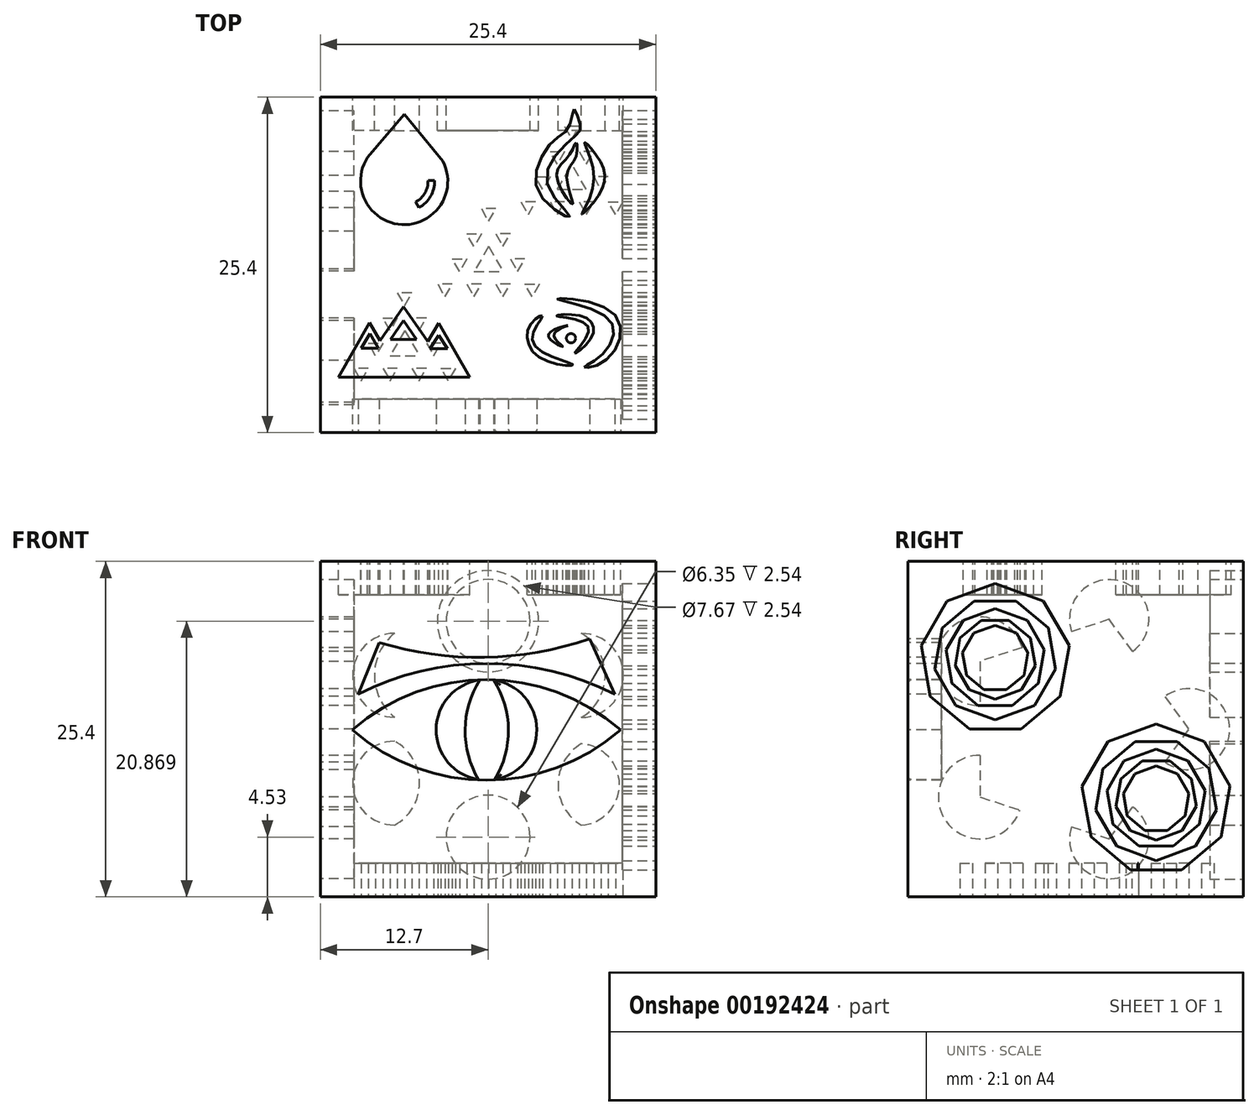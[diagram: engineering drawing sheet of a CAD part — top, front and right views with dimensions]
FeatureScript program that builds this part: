
annotation { "Feature Type Name" : "Feature", "Feature Type Description" : "" }
export const myFeature = defineFeature(function(context is Context, id is Id, definition is map)
    precondition{}
    {
        {
            var Q0;
            Q0=qCreatedBy(makeId("Front.planeOp"),FACE);
            var sketch = newSketch(context, id + "F0", { "sketchPlane" : qUnion([Q0])});
            skLineSegment(sketch, "E0.bottom", {"start": v(12.7, -12.7) * mm, "end": v(-12.7, -12.7) * mm});
            skLineSegment(sketch, "E0.top", {"start": v(12.7, 12.7) * mm, "end": v(-12.7, 12.7) * mm});
            skLineSegment(sketch, "E0.left", {"start": v(12.7, -12.7) * mm, "end": v(12.7, 12.7) * mm});
            skLineSegment(sketch, "E0.right", {"start": v(-12.7, -12.7) * mm, "end": v(-12.7, 12.7) * mm});
            skSolve(sketch);
        }
        {
            var Q0;
            Q0=makeQuery(id+"F0.imprint","IMPRINT",FACE,{"disambiguationData":[TD([[makeQuery(id+"F0.imprint","IMPRINT",EDGE,{"derivedFrom":sQuery(id+"F0.wireOp",EDGE,"E0.bottom")}),-1.0]])]});
            extrude(context, id + "F1", {"entities" : qUnion([Q0]), "depth" : 25.4 * mm});
        }
        {
            var Q0;
            Q0=makeQuery(id+"F1.opExtrude","SWEPT_FACE",FACE,{"disambiguationData":[OSD([sQuery(id+"F0.wireOp",EDGE,"E0.left")])]});
            var sketch = newSketch(context, id + "F2", { "sketchPlane" : qUnion([Q0])});
            skPoint(sketch, "E1.0.midPoint", {"position": v(-14.15, 6.32) * mm});
            skLineSegment(sketch, "E2.0", {"start": v(-2.95, -0.95) * mm, "end": v(-1, -4.32) * mm});
            skLineSegment(sketch, "E2.1", {"start": v(-1, -4.32) * mm, "end": v(-1.67, -8.15) * mm});
            skLineSegment(sketch, "E2.2", {"start": v(-1.67, -8.15) * mm, "end": v(-4.65, -10.65) * mm});
            skLineSegment(sketch, "E2.3", {"start": v(-4.65, -10.65) * mm, "end": v(-8.55, -10.65) * mm});
            skLineSegment(sketch, "E2.4", {"start": v(-8.55, -10.65) * mm, "end": v(-11.53, -8.15) * mm});
            skLineSegment(sketch, "E2.5", {"start": v(-11.53, -8.15) * mm, "end": v(-12.2, -4.32) * mm});
            skLineSegment(sketch, "E2.6", {"start": v(-12.2, -4.32) * mm, "end": v(-10.26, -0.95) * mm});
            skLineSegment(sketch, "E2.7", {"start": v(-10.26, -0.95) * mm, "end": v(-6.6, 0.38) * mm});
            skLineSegment(sketch, "E2.8", {"start": v(-6.6, 0.38) * mm, "end": v(-2.95, -0.95) * mm});
            skPoint(sketch, "E2.0.midPoint", {"position": v(-1.97, -2.63) * mm});
            skLineSegment(sketch, "E3", {"start": v(-5.02, -0.95) * mm, "end": v(-2.59, -2.99) * mm});
            skLineSegment(sketch, "E4", {"start": v(-2.03, -6.11) * mm, "end": v(-2.59, -2.99) * mm});
            skLineSegment(sketch, "E5", {"start": v(-3.62, -8.86) * mm, "end": v(-6.6, -9.95) * mm});
            skLineSegment(sketch, "E6", {"start": v(-2.03, -6.11) * mm, "end": v(-3.62, -8.86) * mm});
            skLineSegment(sketch, "E7", {"start": v(-6.6, -9.95) * mm, "end": v(-9.58, -8.86) * mm});
            skLineSegment(sketch, "E8", {"start": v(-11.17, -6.11) * mm, "end": v(-9.58, -8.86) * mm});
            skLineSegment(sketch, "E9", {"start": v(-11.17, -6.11) * mm, "end": v(-10.62, -3) * mm});
            skLineSegment(sketch, "E10", {"start": v(-8.19, -0.95) * mm, "end": v(-10.62, -3) * mm});
            skLineSegment(sketch, "E11", {"start": v(-8.19, -0.95) * mm, "end": v(-5.02, -0.95) * mm});
            skLineSegment(sketch, "E12", {"start": v(-6.6, -1.53) * mm, "end": v(-4.17, -2.4) * mm});
            skLineSegment(sketch, "E13", {"start": v(-4.17, -2.4) * mm, "end": v(-2.88, -4.65) * mm});
            skLineSegment(sketch, "E14", {"start": v(-3.33, -7.2) * mm, "end": v(-5.3, -8.86) * mm});
            skLineSegment(sketch, "E15", {"start": v(-7.9, -8.86) * mm, "end": v(-9.88, -7.2) * mm});
            skLineSegment(sketch, "E16", {"start": v(-10.33, -4.65) * mm, "end": v(-9.03, -2.41) * mm});
            skLineSegment(sketch, "E17", {"start": v(-9.03, -2.41) * mm, "end": v(-6.6, -1.53) * mm});
            skLineSegment(sketch, "E18", {"start": v(-5.3, -8.86) * mm, "end": v(-7.9, -8.86) * mm});
            skLineSegment(sketch, "E19", {"start": v(-9.88, -7.2) * mm, "end": v(-10.33, -4.65) * mm});
            skLineSegment(sketch, "E20", {"start": v(-2.88, -4.65) * mm, "end": v(-3.33, -7.2) * mm});
            skLineSegment(sketch, "E21", {"start": v(-7.66, -2.41) * mm, "end": v(-5.55, -2.41) * mm});
            skLineSegment(sketch, "E22", {"start": v(-3.93, -3.77) * mm, "end": v(-3.57, -5.84) * mm});
            skLineSegment(sketch, "E23", {"start": v(-4.62, -7.67) * mm, "end": v(-6.6, -8.39) * mm});
            skLineSegment(sketch, "E24", {"start": v(-7.9, -8.86) * mm, "end": v(-7.9, -8.86) * mm});
            skLineSegment(sketch, "E25", {"start": v(-9.27, -3.76) * mm, "end": v(-7.66, -2.41) * mm});
            skLineSegment(sketch, "E26", {"start": v(-6.6, -1.53) * mm, "end": v(-6.6, -1.53) * mm});
            skLineSegment(sketch, "E27", {"start": v(-3.57, -5.84) * mm, "end": v(-4.62, -7.67) * mm});
            skLineSegment(sketch, "E28", {"start": v(-6.6, -8.39) * mm, "end": v(-8.58, -7.67) * mm});
            skLineSegment(sketch, "E29", {"start": v(-9.63, -5.85) * mm, "end": v(-9.27, -3.76) * mm});
            skLineSegment(sketch, "E30", {"start": v(-6.6, -2.8) * mm, "end": v(-4.99, -3.38) * mm});
            skLineSegment(sketch, "E31", {"start": v(-4.13, -4.87) * mm, "end": v(-4.42, -6.56) * mm});
            skLineSegment(sketch, "E32", {"start": v(-5.74, -7.67) * mm, "end": v(-7.46, -7.67) * mm});
            skLineSegment(sketch, "E33", {"start": v(-8.78, -6.57) * mm, "end": v(-9.07, -4.87) * mm});
            skLineSegment(sketch, "E34", {"start": v(-8.22, -3.38) * mm, "end": v(-6.6, -2.8) * mm});
            skLineSegment(sketch, "E35", {"start": v(-4.99, -3.38) * mm, "end": v(-4.13, -4.87) * mm});
            skLineSegment(sketch, "E36", {"start": v(-4.42, -6.56) * mm, "end": v(-5.74, -7.67) * mm});
            skLineSegment(sketch, "E37", {"start": v(-7.46, -7.67) * mm, "end": v(-8.78, -6.57) * mm});
            skLineSegment(sketch, "E38", {"start": v(-9.07, -4.87) * mm, "end": v(-8.22, -3.38) * mm});
            skLineSegment(sketch, "E39.0", {"start": v(-15.13, 9.7) * mm, "end": v(-13.18, 6.34) * mm});
            skLineSegment(sketch, "E39.1", {"start": v(-13.18, 6.34) * mm, "end": v(-13.86, 2.5) * mm});
            skLineSegment(sketch, "E39.2", {"start": v(-13.86, 2.5) * mm, "end": v(-16.84, 0) * mm});
            skLineSegment(sketch, "E39.3", {"start": v(-16.84, 0) * mm, "end": v(-20.73, 0) * mm});
            skLineSegment(sketch, "E39.4", {"start": v(-20.73, 0) * mm, "end": v(-23.71, 2.5) * mm});
            skLineSegment(sketch, "E39.5", {"start": v(-23.71, 2.5) * mm, "end": v(-24.4, 6.33) * mm});
            skLineSegment(sketch, "E39.6", {"start": v(-24.4, 6.33) * mm, "end": v(-22.45, 9.7) * mm});
            skLineSegment(sketch, "E39.7", {"start": v(-22.45, 9.7) * mm, "end": v(-18.79, 11.04) * mm});
            skLineSegment(sketch, "E39.8", {"start": v(-18.79, 11.04) * mm, "end": v(-15.13, 9.7) * mm});
            skPoint(sketch, "E39.0.midPoint", {"position": v(-14.16, 8.02) * mm});
            skLineSegment(sketch, "E40", {"start": v(-17.2, 9.7) * mm, "end": v(-14.77, 7.67) * mm});
            skLineSegment(sketch, "E41", {"start": v(-14.22, 4.54) * mm, "end": v(-14.77, 7.67) * mm});
            skLineSegment(sketch, "E42", {"start": v(-15.8, 1.8) * mm, "end": v(-18.78, 0.7) * mm});
            skLineSegment(sketch, "E43", {"start": v(-14.22, 4.54) * mm, "end": v(-15.8, 1.8) * mm});
            skLineSegment(sketch, "E44", {"start": v(-18.78, 0.7) * mm, "end": v(-21.77, 1.8) * mm});
            skLineSegment(sketch, "E45", {"start": v(-23.35, 4.54) * mm, "end": v(-21.77, 1.8) * mm});
            skLineSegment(sketch, "E46", {"start": v(-23.35, 4.54) * mm, "end": v(-23.35, 4.54) * mm});
            skLineSegment(sketch, "E47", {"start": v(-20.37, 9.7) * mm, "end": v(-17.2, 9.7) * mm});
            skLineSegment(sketch, "E48", {"start": v(-18.79, 9.13) * mm, "end": v(-16.36, 8.24) * mm});
            skLineSegment(sketch, "E49", {"start": v(-16.36, 8.24) * mm, "end": v(-15.06, 6) * mm});
            skLineSegment(sketch, "E50", {"start": v(-22.51, 6) * mm, "end": v(-21.22, 8.24) * mm});
            skLineSegment(sketch, "E51", {"start": v(-21.22, 8.24) * mm, "end": v(-18.79, 9.13) * mm});
            skLineSegment(sketch, "E52", {"start": v(-22.06, 3.46) * mm, "end": v(-22.51, 6) * mm});
            skLineSegment(sketch, "E53", {"start": v(-15.06, 6) * mm, "end": v(-15.51, 3.46) * mm});
            skLineSegment(sketch, "E54", {"start": v(-19.85, 8.24) * mm, "end": v(-17.73, 8.24) * mm});
            skLineSegment(sketch, "E55", {"start": v(-16.12, 6.89) * mm, "end": v(-15.75, 4.81) * mm});
            skLineSegment(sketch, "E56", {"start": v(-16.8, 2.99) * mm, "end": v(-18.78, 2.26) * mm});
            skLineSegment(sketch, "E57", {"start": v(-21.46, 6.89) * mm, "end": v(-19.85, 8.24) * mm});
            skLineSegment(sketch, "E58", {"start": v(-15.75, 4.81) * mm, "end": v(-16.8, 2.99) * mm});
            skLineSegment(sketch, "E59", {"start": v(-18.78, 2.26) * mm, "end": v(-20.77, 2.99) * mm});
            skLineSegment(sketch, "E60", {"start": v(-21.82, 4.8) * mm, "end": v(-21.46, 6.89) * mm});
            skLineSegment(sketch, "E61", {"start": v(-18.79, 7.86) * mm, "end": v(-17.17, 7.27) * mm});
            skLineSegment(sketch, "E62", {"start": v(-16.31, 5.78) * mm, "end": v(-16.6, 4.1) * mm});
            skLineSegment(sketch, "E63", {"start": v(-17.93, 2.99) * mm, "end": v(-19.64, 2.99) * mm});
            skLineSegment(sketch, "E64", {"start": v(-20.96, 4.09) * mm, "end": v(-21.26, 5.78) * mm});
            skLineSegment(sketch, "E65", {"start": v(-17.17, 7.27) * mm, "end": v(-16.31, 5.78) * mm});
            skLineSegment(sketch, "E66", {"start": v(-16.6, 4.1) * mm, "end": v(-17.93, 2.99) * mm});
            skLineSegment(sketch, "E67", {"start": v(-19.64, 2.99) * mm, "end": v(-20.96, 4.09) * mm});
            skLineSegment(sketch, "E68", {"start": v(-21.26, 5.78) * mm, "end": v(-20.4, 7.27) * mm});
            skPoint(sketch, "E69.endSnap0", {"position": v(-6.6, -8.86) * mm});
            skPoint(sketch, "E70.orphan", {"position": v(-11.17, -6.11) * mm});
            skPoint(sketch, "E71.orphan", {"position": v(-9.58, -8.86) * mm});
            skLineSegment(sketch, "E72.trimOffspring", {"start": v(-7.89, -8.86) * mm, "end": v(-7.9, -8.86) * mm});
            skLineSegment(sketch, "E73.trimOffspring", {"start": v(-8.58, -7.67) * mm, "end": v(-9.63, -5.85) * mm});
            skLineSegment(sketch, "E74.trimOffspring", {"start": v(-5.55, -2.41) * mm, "end": v(-3.93, -3.77) * mm});
            skLineSegment(sketch, "E75", {"start": v(-20.37, 9.7) * mm, "end": v(-22.8, 7.66) * mm});
            skLineSegment(sketch, "E76", {"start": v(-23.35, 4.54) * mm, "end": v(-22.8, 7.66) * mm});
            skLineSegment(sketch, "E77.trimOffspring", {"start": v(-20.77, 2.99) * mm, "end": v(-21.82, 4.8) * mm});
            skLineSegment(sketch, "E78.trimOffspring", {"start": v(-17.73, 8.24) * mm, "end": v(-16.12, 6.89) * mm});
            skLineSegment(sketch, "E79", {"start": v(-20.4, 7.27) * mm, "end": v(-18.79, 7.86) * mm});
            skLineSegment(sketch, "E80", {"start": v(-22.06, 3.46) * mm, "end": v(-20.08, 1.8) * mm});
            skLineSegment(sketch, "E81", {"start": v(-20.08, 1.8) * mm, "end": v(-17.5, 1.8) * mm});
            skLineSegment(sketch, "E82", {"start": v(-15.51, 3.46) * mm, "end": v(-17.5, 1.8) * mm});
            skSolve(sketch);
        }
        {
            var Q0;
            Q0=makeQuery(id+"F2.imprint","IMPRINT",FACE,{"disambiguationData":[TD([[makeQuery(id+"F2.imprint","IMPRINT",EDGE,{"derivedFrom":sQuery(id+"F2.wireOp",EDGE,"E2.0")}),-1.0]])]});
            var Q1;
            {var subQ10=sQuery(id+"F2.wireOp",EDGE,"E13");Q1=makeQuery(id+"F2.imprint","IMPRINT",FACE,{"disambiguationData":[TD([[makeQuery(id+"F2.imprint","IMPRINT",EDGE,{"derivedFrom":subQ10}),-1.0]])]});}
            var Q2;
            Q2=makeQuery(id+"F2.imprint","IMPRINT",FACE,{"disambiguationData":[TD([[makeQuery(id+"F2.imprint","IMPRINT",EDGE,{"derivedFrom":sQuery(id+"F2.wireOp",EDGE,"E30")}),-1.0]])]});
            extrude(context, id + "F3", {"entities" : qUnion([Q0, Q1, Q2]), "operationType" : NewBodyOperationType.REMOVE, "oppositeDirection" : true, "depth" : 2.54 * mm});
        }
        {
            var Q0;
            Q0=makeQuery(id+"F2.imprint","IMPRINT",FACE,{"disambiguationData":[TD([[makeQuery(id+"F2.imprint","IMPRINT",EDGE,{"derivedFrom":sQuery(id+"F2.wireOp",EDGE,"E39.0")}),-1.0]])]});
            var Q1;
            Q1=makeQuery(id+"F2.imprint","IMPRINT",FACE,{"disambiguationData":[TD([[makeQuery(id+"F2.imprint","IMPRINT",EDGE,{"derivedFrom":sQuery(id+"F2.wireOp",EDGE,"E48")}),-1.0]])]});
            var Q2;
            Q2=makeQuery(id+"F2.imprint","IMPRINT",FACE,{"disambiguationData":[TD([[makeQuery(id+"F2.imprint","IMPRINT",EDGE,{"derivedFrom":sQuery(id+"F2.wireOp",EDGE,"E61")}),-1.0]])]});
            extrude(context, id + "F4", {"entities" : qUnion([Q0, Q1, Q2]), "operationType" : NewBodyOperationType.REMOVE, "oppositeDirection" : true, "depth" : 2.54 * mm});
        }
        {
            var Q0;
            {var subQ0=sQuery(id+"F0.wireOp",EDGE,"Xz3h7y4A-9vBR-dhRj-rXEC-ED03mauQ3q4K");var subQ1=sQuery(id+"F0.wireOp",EDGE,"V4NEk3Ng-o78i-laLm-4UWv-CYlOKSxuC9OK");var subQ2=sQuery(id+"F0.wireOp",EDGE,"mu0T6BV1-LyfI-ftHM-lo53-aBSG0DslEf0h");var subQ3=sQuery(id+"F0.wireOp",EDGE,"n15qH9Pv-QceR-e55J-xRJA-4Z23myPxkwqh");var subQ4=makeQuery(id+"F0.imprint","INTERSECT",VERTEX,{"derivedFrom":[subQ3,subQ2,subQ1,subQ0]});var subQ5=sQuery(id+"F0.wireOp",EDGE,"ffxhiTFt-cJhM-8va8-o5as-TkoKFeYBlZlv");var subQ7=makeQuery(id+"F0.imprint","INTERSECT",VERTEX,{"disambiguationData":[OD(1.0)],"derivedFrom":[subQ5,subQ3]});var subQ8=makeQuery(id+"F0.imprint","INTERSECT",VERTEX,{"disambiguationData":[OD(0.0)],"derivedFrom":[subQ5,subQ3]});var subQ9=sQuery(id+"F0.wireOp",EDGE,"c9E78YFX-uoQ2-b4qo-jO5v-nr7yERCXFzAn");var subQ10=sQuery(id+"F0.wireOp",EDGE,"twlR4qeh-pLNo-oQQC-zrHb-Cr716ABeDlEO");var subQ11=sQuery(id+"F0.wireOp",EDGE,"i75eDPNT-zkQp-M9GV-G1os-5atVE6ZioN9H");var subQ12=sQuery(id+"F0.wireOp",EDGE,"Tw14qS9G-7LKB-szX9-mnEh-GGdI6fmKwQ57");Q0=makeQuery(id+"FcBMYDftipxSYez_0.boolean.opBoolean","MERGE",FACE,{"derivedFrom":[makeQuery(id+"FdykabLyeeUPw6N_0.boolean.opBoolean","MERGE",FACE,{"derivedFrom":[makeQuery(id+"F1.opExtrude","CAP_FACE",FACE,{"disambiguationData":[OSD([sQuery(id+"F0.wireOp",EDGE,"E0.bottom"),sQuery(id+"F0.wireOp",EDGE,"E0.top"),sQuery(id+"F0.wireOp",EDGE,"E0.left"),sQuery(id+"F0.wireOp",EDGE,"E0.right"),subQ5,subQ3,subQ12,subQ11,subQ10,subQ9])],"isStart":true}),makeQuery(id+"FdykabLyeeUPw6N_0.opExtrude","CAP_FACE",FACE,{"disambiguationData":[OSD([subQ12,subQ11,subQ10,subQ9])],"isStart":true})]}),makeQuery(id+"FcBMYDftipxSYez_0.opExtrude","CAP_FACE",FACE,{"disambiguationData":[OSD([subQ5,subQ3,subQ2]),TDD([makeQuery(id+"F0.imprint","IMPRINT",EDGE,{"disambiguationData":[TD([[subQ8,-1.0]])],"derivedFrom":subQ5}),makeQuery(id+"F0.imprint","IMPRINT",EDGE,{"disambiguationData":[TD([[subQ8,1.0]])],"derivedFrom":subQ3}),makeQuery(id+"F0.imprint","IMPRINT",EDGE,{"disambiguationData":[TD([[subQ4,-1.0]])],"derivedFrom":subQ2})])],"isStart":true}),makeQuery(id+"FcBMYDftipxSYez_0.opExtrude","CAP_FACE",FACE,{"disambiguationData":[OSD([subQ5,subQ3,subQ2]),TDD([makeQuery(id+"F0.imprint","IMPRINT",EDGE,{"disambiguationData":[TD([[subQ7,1.0]])],"derivedFrom":subQ5}),makeQuery(id+"F0.imprint","IMPRINT",EDGE,{"disambiguationData":[TD([[subQ7,-1.0]])],"derivedFrom":subQ3}),makeQuery(id+"F0.imprint","IMPRINT",EDGE,{"disambiguationData":[TD([[subQ4,1.0]])],"derivedFrom":subQ2})])],"isStart":true})]});}
            var sketch = newSketch(context, id + "F5", { "sketchPlane" : qUnion([Q0])});
            skPoint(sketch, "E83.cCircle.perimeterSnap0", {"position": v(12.7, 0) * mm});
            skPoint(sketch, "E83.0.midPoint", {"position": v(7.08, 0) * mm});
            skPoint(sketch, "E83.0.midPoint.positionSnap0", {"position": v(12.7, 0) * mm});
            skCircle(sketch, "E84", {"center": v(0, 8.17) * mm, "radius": 3.17 * mm});
            skCircle(sketch, "E85", {"center": v(7.08, 4.08) * mm, "radius": 3.18 * mm});
            skCircle(sketch, "E86", {"center": v(7.08, -4.08) * mm, "radius": 3.18 * mm});
            skCircle(sketch, "E87", {"center": v(0, -8.17) * mm, "radius": 3.18 * mm});
            skCircle(sketch, "E88", {"center": v(-6.87, -4.19) * mm, "radius": 3.08 * mm});
            skCircle(sketch, "E89", {"center": v(-7.08, 4.07) * mm, "radius": 3.18 * mm});
            skArc(sketch, "E90", {"start": v(7.08, 0.9) * mm, "mid": v(8.6, 4.08) * mm, "end": v(7.08, 7.26) * mm});
            skArc(sketch, "E91", {"start": v(7.08, -0.9) * mm, "mid": v(5.18, -4.08) * mm, "end": v(7.08, -7.26) * mm});
            skArc(sketch, "E92", {"start": v(-7.08, -7.26) * mm, "mid": v(-5.3, -4.19) * mm, "end": v(-7.08, -1.11) * mm});
            skArc(sketch, "E93", {"start": v(-7.08, 7.24) * mm, "mid": v(-8.86, 4.07) * mm, "end": v(-7.08, 0.9) * mm});
            skCircle(sketch, "E94", {"center": v(0, 8.17) * mm, "radius": 3.84 * mm});
            skSolve(sketch);
        }
        {
            var Q0;
            Q0=makeQuery(id+"F5.imprint","IMPRINT",FACE,{"disambiguationData":[TD([[makeQuery(id+"F5.imprint","IMPRINT",EDGE,{"derivedFrom":sQuery(id+"F5.wireOp",EDGE,"E87")}),1.0]])]});
            extrude(context, id + "F6", {"entities" : qUnion([Q0]), "operationType" : NewBodyOperationType.REMOVE, "oppositeDirection" : true, "depth" : 2.54 * mm});
        }
        {
            var Q0;
            {var subQ0=sQuery(id+"F5.wireOp",EDGE,"E91");Q0=makeQuery(id+"F5.imprint","IMPRINT",FACE,{"disambiguationData":[TD([[makeQuery(id+"F5.imprint","IMPRINT",EDGE,{"derivedFrom":subQ0}),1.0]])]});}
            extrude(context, id + "F7", {"entities" : qUnion([Q0]), "operationType" : NewBodyOperationType.REMOVE, "oppositeDirection" : true, "depth" : 2.54 * mm});
        }
        {
            var Q0;
            {var subQ0=sQuery(id+"F5.wireOp",EDGE,"E90");Q0=makeQuery(id+"F5.imprint","IMPRINT",FACE,{"disambiguationData":[TD([[makeQuery(id+"F5.imprint","IMPRINT",EDGE,{"derivedFrom":subQ0}),-1.0]])]});}
            var Q1;
            {var subQ0=sQuery(id+"F5.wireOp",EDGE,"E93");Q1=makeQuery(id+"F5.imprint","IMPRINT",FACE,{"disambiguationData":[TD([[makeQuery(id+"F5.imprint","IMPRINT",EDGE,{"derivedFrom":subQ0}),-1.0]])]});}
            var Q2;
            {var subQ0=sQuery(id+"F5.wireOp",EDGE,"E92");Q2=makeQuery(id+"F5.imprint","IMPRINT",FACE,{"disambiguationData":[TD([[makeQuery(id+"F5.imprint","IMPRINT",EDGE,{"derivedFrom":subQ0}),1.0]])]});}
            extrude(context, id + "F8", {"entities" : qUnion([Q0, Q1, Q2]), "operationType" : NewBodyOperationType.REMOVE, "oppositeDirection" : true, "depth" : 2.54 * mm});
        }
        {
            var Q0;
            Q0=makeQuery(id+"F5.imprint","IMPRINT",FACE,{"disambiguationData":[TD([[makeQuery(id+"F5.imprint","IMPRINT",EDGE,{"derivedFrom":sQuery(id+"F5.wireOp",EDGE,"E84")}),-1.0]])]});
            extrude(context, id + "F9", {"entities" : qUnion([Q0]), "operationType" : NewBodyOperationType.REMOVE, "oppositeDirection" : true, "depth" : 2.54 * mm});
        }
        {
            var Q0;
            Q0=makeQuery(id+"F1.opExtrude","SWEPT_FACE",FACE,{"disambiguationData":[OSD([sQuery(id+"F0.wireOp",EDGE,"E0.top")])]});
            var sketch = newSketch(context, id + "F10", { "sketchPlane" : qUnion([Q0])});
            skLineSegment(sketch, "E95", {"start": v(-12.7, -12.7) * mm, "end": v(12.7, -12.7) * mm});
            skArc(sketch, "E96", {"start": v(-8.57, -3.9) * mm, "mid": v(-8.63, -3.96) * mm, "end": v(-8.68, -4.02) * mm});
            skLineSegment(sketch, "E97", {"start": v(-9.12, -4.55) * mm, "end": v(-6.35, -1.29) * mm});
            skLineSegment(sketch, "E98", {"start": v(-6.35, -1.29) * mm, "end": v(-3.4, -4.86) * mm});
            skArc(sketch, "E99.trimOffspring", {"start": v(-9.12, -4.55) * mm, "mid": v(-6.53, -9.65) * mm, "end": v(-3.4, -4.86) * mm});
            skArc(sketch, "E100", {"start": v(-5.24, -8.37) * mm, "mid": v(-4.35, -7.5) * mm, "end": v(-4.04, -6.32) * mm});
            skArc(sketch, "E101", {"start": v(-5.48, -7.93) * mm, "mid": v(-4.79, -7.26) * mm, "end": v(-4.54, -6.32) * mm});
            skLineSegment(sketch, "E102", {"start": v(-5.48, -7.93) * mm, "end": v(-5.24, -8.37) * mm});
            skLineSegment(sketch, "E103", {"start": v(-4.54, -6.32) * mm, "end": v(-4.04, -6.32) * mm});
            skPoint(sketch, "E104.7.internal.snap0", {"position": v(7, -2.15) * mm});
            skFitSpline(sketch, "E104", {"points": [v(6.51, -0.92) * mm, v(7, -2.15) * mm, v(6.66, -2.88) * mm, v(4.44, -6.25) * mm, v(6.18, -9.05) * mm, v(3.84, -7.23) * mm, v(4.8, -3.48) * mm, v(6.18, -2.15) * mm, v(6.51, -0.92) * mm]});
            skPoint(sketch, "E105.1.internal.snap0", {"position": v(6.82, -4.49) * mm});
            skFitSpline(sketch, "E105", {"points": [v(6.67, -3.44) * mm, v(6.67, -4.49) * mm, v(5.96, -6) * mm, v(6.4, -8.1) * mm, v(5.2, -5.95) * mm, v(6.18, -4.35) * mm, v(6.67, -3.44) * mm]});
            skFitSpline(sketch, "E106", {"points": [v(8.51, -4.9) * mm, v(8.54, -7.15) * mm, v(7.13, -8.86) * mm, v(8.02, -6.28) * mm, v(7.32, -3.43) * mm, v(8.51, -4.9) * mm]});
            skLineSegment(sketch, "E107.0", {"start": v(-2.64, -21.2) * mm, "end": v(-10.06, -21.2) * mm});
            skLineSegment(sketch, "E107.1", {"start": v(-8.17, -18.45) * mm, "end": v(-6.4, -15.87) * mm});
            skLineSegment(sketch, "E107.2", {"start": v(-6.4, -15.87) * mm, "end": v(-4.55, -18.5) * mm});
            skPoint(sketch, "E107.0.midPoint", {"position": v(-6.35, -21.2) * mm});
            skLineSegment(sketch, "E108.0", {"start": v(-1.37, -21.2) * mm, "end": v(-6.1, -21.2) * mm});
            skLineSegment(sketch, "E108.1", {"start": v(-4.55, -18.5) * mm, "end": v(-3.74, -17.1) * mm});
            skLineSegment(sketch, "E108.2", {"start": v(-3.74, -17.1) * mm, "end": v(-1.37, -21.2) * mm});
            skPoint(sketch, "E108.0.midPoint", {"position": v(-3.74, -21.2) * mm});
            skLineSegment(sketch, "E109.0", {"start": v(-6.59, -21.2) * mm, "end": v(-11.33, -21.2) * mm});
            skLineSegment(sketch, "E109.1", {"start": v(-11.33, -21.2) * mm, "end": v(-8.96, -17.08) * mm});
            skLineSegment(sketch, "E109.2", {"start": v(-8.96, -17.08) * mm, "end": v(-8.17, -18.45) * mm});
            skPoint(sketch, "E109.0.midPoint", {"position": v(-8.96, -21.2) * mm});
            skLineSegment(sketch, "E110", {"start": v(-6.4, -16.9) * mm, "end": v(-7.4, -18.34) * mm});
            skLineSegment(sketch, "E111", {"start": v(-7.4, -18.34) * mm, "end": v(-5.42, -18.34) * mm});
            skLineSegment(sketch, "E112", {"start": v(-5.42, -18.34) * mm, "end": v(-6.4, -16.9) * mm});
            skLineSegment(sketch, "E113", {"start": v(-8.95, -17.9) * mm, "end": v(-9.6, -19.02) * mm});
            skLineSegment(sketch, "E114", {"start": v(-9.6, -19.02) * mm, "end": v(-8.32, -19.02) * mm});
            skLineSegment(sketch, "E115", {"start": v(-8.32, -19.02) * mm, "end": v(-8.95, -17.9) * mm});
            skLineSegment(sketch, "E116", {"start": v(-3.74, -18.04) * mm, "end": v(-4.4, -19.05) * mm});
            skLineSegment(sketch, "E117", {"start": v(-4.4, -19.05) * mm, "end": v(-3.08, -19.05) * mm});
            skLineSegment(sketch, "E118", {"start": v(-3.08, -19.05) * mm, "end": v(-3.74, -18.04) * mm});
            skPoint(sketch, "E119.1.internal.snap0", {"position": v(7.6, -18.57) * mm});
            skPoint(sketch, "E119.4.internal.snap0", {"position": v(7.29, -18.52) * mm});
            skFitSpline(sketch, "E119", {"points": [v(6.56, -19.4) * mm, v(7.6, -17.42) * mm, v(5.2, -16.55) * mm, v(7.29, -16.65) * mm, v(7.84, -18.17) * mm, v(6.56, -19.4) * mm]});
            skFitSpline(sketch, "E120", {"points": [v(4.11, -16.56) * mm, v(3.14, -17.33) * mm, v(4, -19.77) * mm, v(6.42, -20.24) * mm, v(3.4, -18.58) * mm, v(4.11, -16.56) * mm]});
            skPoint(sketch, "E121.3.internal.snap0", {"position": v(6.12, -17.98) * mm});
            skFitSpline(sketch, "E121", {"points": [v(6.05, -17.29) * mm, v(4.56, -18.02) * mm, v(5.67, -18.9) * mm, v(4.98, -17.98) * mm, v(6.05, -17.29) * mm]});
            skFitSpline(sketch, "E122", {"points": [v(7.28, -20.44) * mm, v(8.92, -19.91) * mm, v(9.53, -16.38) * mm, v(5.25, -15.28) * mm, v(9.17, -16.82) * mm, v(8.51, -19.6) * mm, v(7.28, -20.44) * mm]});
            skCircle(sketch, "E123", {"center": v(6.28, -18.25) * mm, "radius": 0.35 * mm});
            skSolve(sketch);
        }
        {
            var Q0;
            {var subQ1=sQuery(id+"F10.wireOp",EDGE,"E98");Q0=makeQuery(id+"F10.imprint","IMPRINT",FACE,{"disambiguationData":[TD([[makeQuery(id+"F10.imprint","IMPRINT",EDGE,{"derivedFrom":subQ1}),-1.0]])]});}
            extrude(context, id + "F11", {"entities" : qUnion([Q0]), "operationType" : NewBodyOperationType.REMOVE, "oppositeDirection" : true, "depth" : 2.54 * mm});
        }
        {
            var Q0;
            Q0=makeQuery(id+"F10.imprint","IMPRINT",FACE,{"disambiguationData":[TD([[makeQuery(id+"F10.imprint","IMPRINT",EDGE,{"derivedFrom":sQuery(id+"F10.wireOp",EDGE,"E104")}),-1.0]])]});
            var Q1;
            Q1=makeQuery(id+"F10.imprint","IMPRINT",FACE,{"disambiguationData":[TD([[makeQuery(id+"F10.imprint","IMPRINT",EDGE,{"derivedFrom":sQuery(id+"F10.wireOp",EDGE,"E106")}),-1.0]])]});
            extrude(context, id + "F12", {"entities" : qUnion([Q0, Q1]), "operationType" : NewBodyOperationType.REMOVE, "oppositeDirection" : true, "depth" : 2.54 * mm});
        }
        {
            var Q0;
            Q0=makeQuery(id+"F10.imprint","IMPRINT",FACE,{"disambiguationData":[TD([[makeQuery(id+"F10.imprint","IMPRINT",EDGE,{"derivedFrom":sQuery(id+"F10.wireOp",EDGE,"E105")}),-1.0]])]});
            extrude(context, id + "F13", {"entities" : qUnion([Q0]), "operationType" : NewBodyOperationType.REMOVE, "oppositeDirection" : true, "depth" : 2.54 * mm});
        }
        {
            var Q0;
            {var subQ3=sQuery(id+"F10.wireOp",EDGE,"E107.0");Q0=makeQuery(id+"F10.imprint","IMPRINT",FACE,{"disambiguationData":[TD([[makeQuery(id+"F10.imprint","IMPRINT",EDGE,{"derivedFrom":subQ3}),-1.0]])]});}
            extrude(context, id + "F14", {"entities" : qUnion([Q0]), "operationType" : NewBodyOperationType.REMOVE, "oppositeDirection" : true, "depth" : 2.54 * mm});
        }
        {
            var Q0;
            Q0=makeQuery(id+"F10.imprint","IMPRINT",FACE,{"disambiguationData":[TD([[makeQuery(id+"F10.imprint","IMPRINT",EDGE,{"derivedFrom":sQuery(id+"F10.wireOp",EDGE,"E119")}),-1.0]])]});
            var Q1;
            Q1=makeQuery(id+"F10.imprint","IMPRINT",FACE,{"disambiguationData":[TD([[makeQuery(id+"F10.imprint","IMPRINT",EDGE,{"derivedFrom":sQuery(id+"F10.wireOp",EDGE,"E121")}),1.0]])]});
            var Q2;
            Q2=makeQuery(id+"F10.imprint","IMPRINT",FACE,{"disambiguationData":[TD([[makeQuery(id+"F10.imprint","IMPRINT",EDGE,{"derivedFrom":sQuery(id+"F10.wireOp",EDGE,"E120")}),1.0]])]});
            var Q3;
            Q3=makeQuery(id+"F10.imprint","IMPRINT",FACE,{"disambiguationData":[TD([[makeQuery(id+"F10.imprint","IMPRINT",EDGE,{"derivedFrom":sQuery(id+"F10.wireOp",EDGE,"E122")}),1.0]])]});
            extrude(context, id + "F15", {"entities" : qUnion([Q0, Q1, Q2, Q3]), "operationType" : NewBodyOperationType.REMOVE, "oppositeDirection" : true, "depth" : 2.54 * mm});
        }
        {
            var Q0;
            Q0=makeQuery(id+"F10.imprint","IMPRINT",FACE,{"disambiguationData":[TD([[makeQuery(id+"F10.imprint","IMPRINT",EDGE,{"derivedFrom":sQuery(id+"F10.wireOp",EDGE,"E123")}),1.0]])]});
            extrude(context, id + "F16", {"entities" : qUnion([Q0]), "operationType" : NewBodyOperationType.REMOVE, "oppositeDirection" : true, "depth" : 2.54 * mm});
        }
        {
            var Q0;
            Q0=makeQuery(id+"F1.opExtrude","SWEPT_FACE",FACE,{"disambiguationData":[OSD([sQuery(id+"F0.wireOp",EDGE,"E0.bottom")])]});
            var sketch = newSketch(context, id + "F17", { "sketchPlane" : qUnion([Q0])});
            skLineSegment(sketch, "E124.0", {"start": v(1.95, 8.9) * mm, "end": v(10.75, 8.9) * mm});
            skLineSegment(sketch, "E124.1", {"start": v(10.75, 8.9) * mm, "end": v(6.35, 1.27) * mm});
            skLineSegment(sketch, "E124.2", {"start": v(6.35, 1.27) * mm, "end": v(1.95, 8.9) * mm});
            skPoint(sketch, "E124.0.midPoint", {"position": v(6.35, 8.9) * mm});
            skPoint(sketch, "E125.0.midPoint", {"position": v(0, 15.24) * mm});
            skPoint(sketch, "E126.0.midPoint", {"position": v(-6.35, 21.59) * mm});
            skLineSegment(sketch, "E127", {"start": v(8.55, 5.08) * mm, "end": v(4.15, 5.08) * mm});
            skLineSegment(sketch, "E128", {"start": v(4.15, 5.08) * mm, "end": v(6.35, 8.9) * mm});
            skLineSegment(sketch, "E129", {"start": v(8.55, 5.08) * mm, "end": v(6.35, 8.9) * mm});
            skLineSegment(sketch, "E130", {"start": v(6.35, 5.08) * mm, "end": v(7.45, 3.17) * mm});
            skLineSegment(sketch, "E131", {"start": v(7.45, 3.17) * mm, "end": v(5.25, 3.17) * mm});
            skLineSegment(sketch, "E132", {"start": v(5.25, 3.17) * mm, "end": v(6.35, 5.08) * mm});
            skLineSegment(sketch, "E133", {"start": v(5.25, 6.99) * mm, "end": v(4.15, 8.9) * mm});
            skLineSegment(sketch, "E134", {"start": v(4.15, 8.9) * mm, "end": v(3.05, 6.99) * mm});
            skLineSegment(sketch, "E135", {"start": v(3.05, 6.99) * mm, "end": v(5.25, 6.99) * mm});
            skLineSegment(sketch, "E136", {"start": v(7.45, 6.99) * mm, "end": v(9.65, 6.99) * mm});
            skLineSegment(sketch, "E137", {"start": v(9.65, 6.99) * mm, "end": v(8.55, 8.9) * mm});
            skLineSegment(sketch, "E138", {"start": v(8.55, 8.9) * mm, "end": v(7.45, 6.99) * mm});
            skLineSegment(sketch, "E139", {"start": v(8.55, 6.99) * mm, "end": v(9.1, 6.03) * mm});
            skLineSegment(sketch, "E140", {"start": v(9.1, 6.03) * mm, "end": v(8, 6.03) * mm});
            skLineSegment(sketch, "E141", {"start": v(8, 6.03) * mm, "end": v(8.55, 6.99) * mm});
            skLineSegment(sketch, "E142", {"start": v(9.1, 7.94) * mm, "end": v(10.2, 7.94) * mm});
            skLineSegment(sketch, "E143", {"start": v(10.2, 7.94) * mm, "end": v(9.65, 8.9) * mm});
            skLineSegment(sketch, "E144", {"start": v(9.65, 8.89) * mm, "end": v(9.1, 7.94) * mm});
            skLineSegment(sketch, "E145", {"start": v(8, 7.94) * mm, "end": v(6.9, 7.94) * mm});
            skLineSegment(sketch, "E146", {"start": v(6.9, 7.94) * mm, "end": v(7.45, 8.9) * mm});
            skLineSegment(sketch, "E147", {"start": v(7.45, 8.9) * mm, "end": v(8, 7.94) * mm});
            skLineSegment(sketch, "E148", {"start": v(5.8, 7.94) * mm, "end": v(4.7, 7.94) * mm});
            skLineSegment(sketch, "E149", {"start": v(4.7, 7.94) * mm, "end": v(5.25, 8.9) * mm});
            skLineSegment(sketch, "E150", {"start": v(5.25, 8.9) * mm, "end": v(5.8, 7.94) * mm});
            skLineSegment(sketch, "E151", {"start": v(3.6, 7.94) * mm, "end": v(2.5, 7.94) * mm});
            skLineSegment(sketch, "E152", {"start": v(2.5, 7.94) * mm, "end": v(3.05, 8.9) * mm});
            skLineSegment(sketch, "E153", {"start": v(3.05, 8.9) * mm, "end": v(3.6, 7.94) * mm});
            skLineSegment(sketch, "E154", {"start": v(4.15, 6.99) * mm, "end": v(3.6, 6.03) * mm});
            skLineSegment(sketch, "E155", {"start": v(3.6, 6.03) * mm, "end": v(4.7, 6.03) * mm});
            skLineSegment(sketch, "E156", {"start": v(4.7, 6.03) * mm, "end": v(4.15, 6.99) * mm});
            skLineSegment(sketch, "E157", {"start": v(5.8, 4.13) * mm, "end": v(5.25, 5.08) * mm});
            skLineSegment(sketch, "E158", {"start": v(5.25, 5.08) * mm, "end": v(4.7, 4.13) * mm});
            skLineSegment(sketch, "E159", {"start": v(4.7, 4.13) * mm, "end": v(5.8, 4.13) * mm});
            skLineSegment(sketch, "E160", {"start": v(6.9, 4.13) * mm, "end": v(7.45, 5.08) * mm});
            skLineSegment(sketch, "E161", {"start": v(7.45, 5.08) * mm, "end": v(8, 4.13) * mm});
            skLineSegment(sketch, "E162", {"start": v(8, 4.13) * mm, "end": v(6.9, 4.13) * mm});
            skLineSegment(sketch, "E163", {"start": v(6.35, 3.17) * mm, "end": v(6.9, 2.22) * mm});
            skLineSegment(sketch, "E164", {"start": v(6.9, 2.22) * mm, "end": v(5.8, 2.22) * mm});
            skLineSegment(sketch, "E165", {"start": v(5.8, 2.22) * mm, "end": v(6.35, 3.17) * mm});
            skLineSegment(sketch, "E166.0", {"start": v(-4.36, 15.1) * mm, "end": v(4.44, 15.1) * mm});
            skLineSegment(sketch, "E166.1", {"start": v(4.44, 15.1) * mm, "end": v(0.04, 7.49) * mm});
            skLineSegment(sketch, "E166.2", {"start": v(0.04, 7.49) * mm, "end": v(-4.36, 15.1) * mm});
            skPoint(sketch, "E166.0.midPoint", {"position": v(0.04, 15.1) * mm});
            skLineSegment(sketch, "E167", {"start": v(2.24, 11.3) * mm, "end": v(-2.16, 11.3) * mm});
            skLineSegment(sketch, "E168", {"start": v(-2.16, 11.3) * mm, "end": v(0.04, 15.1) * mm});
            skLineSegment(sketch, "E169", {"start": v(2.24, 11.3) * mm, "end": v(0.04, 15.1) * mm});
            skLineSegment(sketch, "E170", {"start": v(0.04, 11.3) * mm, "end": v(1.14, 9.4) * mm});
            skLineSegment(sketch, "E171", {"start": v(1.14, 9.4) * mm, "end": v(-1.06, 9.4) * mm});
            skLineSegment(sketch, "E172", {"start": v(-1.06, 9.4) * mm, "end": v(0.04, 11.3) * mm});
            skLineSegment(sketch, "E173", {"start": v(-1.06, 13.2) * mm, "end": v(-2.16, 15.1) * mm});
            skLineSegment(sketch, "E174", {"start": v(-2.16, 15.1) * mm, "end": v(-3.26, 13.2) * mm});
            skLineSegment(sketch, "E175", {"start": v(-3.26, 13.2) * mm, "end": v(-1.06, 13.2) * mm});
            skLineSegment(sketch, "E176", {"start": v(1.14, 13.2) * mm, "end": v(3.34, 13.2) * mm});
            skLineSegment(sketch, "E177", {"start": v(3.34, 13.2) * mm, "end": v(2.24, 15.1) * mm});
            skLineSegment(sketch, "E178", {"start": v(2.24, 15.1) * mm, "end": v(1.14, 13.2) * mm});
            skLineSegment(sketch, "E179", {"start": v(2.24, 13.2) * mm, "end": v(2.79, 12.25) * mm});
            skLineSegment(sketch, "E180", {"start": v(2.79, 12.25) * mm, "end": v(1.69, 12.25) * mm});
            skLineSegment(sketch, "E181", {"start": v(1.69, 12.25) * mm, "end": v(2.24, 13.2) * mm});
            skLineSegment(sketch, "E182", {"start": v(2.79, 14.16) * mm, "end": v(3.89, 14.16) * mm});
            skLineSegment(sketch, "E183", {"start": v(3.89, 14.16) * mm, "end": v(3.34, 15.1) * mm});
            skLineSegment(sketch, "E184", {"start": v(3.34, 15.1) * mm, "end": v(2.79, 14.16) * mm});
            skLineSegment(sketch, "E185", {"start": v(1.69, 14.16) * mm, "end": v(0.59, 14.16) * mm});
            skLineSegment(sketch, "E186", {"start": v(0.59, 14.16) * mm, "end": v(1.14, 15.1) * mm});
            skLineSegment(sketch, "E187", {"start": v(1.14, 15.1) * mm, "end": v(1.69, 14.16) * mm});
            skLineSegment(sketch, "E188", {"start": v(-0.51, 14.16) * mm, "end": v(-1.61, 14.16) * mm});
            skLineSegment(sketch, "E189", {"start": v(-1.61, 14.16) * mm, "end": v(-1.06, 15.1) * mm});
            skLineSegment(sketch, "E190", {"start": v(-1.06, 15.1) * mm, "end": v(-0.51, 14.16) * mm});
            skLineSegment(sketch, "E191", {"start": v(-2.71, 14.16) * mm, "end": v(-3.8, 14.16) * mm});
            skLineSegment(sketch, "E192", {"start": v(-3.8, 14.16) * mm, "end": v(-3.26, 15.1) * mm});
            skLineSegment(sketch, "E193", {"start": v(-3.26, 15.1) * mm, "end": v(-2.71, 14.16) * mm});
            skLineSegment(sketch, "E194", {"start": v(-2.16, 13.2) * mm, "end": v(-2.71, 12.25) * mm});
            skLineSegment(sketch, "E195", {"start": v(-2.71, 12.25) * mm, "end": v(-1.61, 12.25) * mm});
            skLineSegment(sketch, "E196", {"start": v(-1.61, 12.25) * mm, "end": v(-2.16, 13.2) * mm});
            skLineSegment(sketch, "E197", {"start": v(-0.51, 10.35) * mm, "end": v(-1.06, 11.3) * mm});
            skLineSegment(sketch, "E198", {"start": v(-1.06, 11.3) * mm, "end": v(-1.61, 10.35) * mm});
            skLineSegment(sketch, "E199", {"start": v(-1.61, 10.35) * mm, "end": v(-0.51, 10.35) * mm});
            skLineSegment(sketch, "E200", {"start": v(0.59, 10.35) * mm, "end": v(1.14, 11.3) * mm});
            skLineSegment(sketch, "E201", {"start": v(1.14, 11.3) * mm, "end": v(1.69, 10.35) * mm});
            skLineSegment(sketch, "E202", {"start": v(1.69, 10.35) * mm, "end": v(0.59, 10.35) * mm});
            skLineSegment(sketch, "E203", {"start": v(0.04, 9.4) * mm, "end": v(0.59, 8.44) * mm});
            skLineSegment(sketch, "E204", {"start": v(0.59, 8.44) * mm, "end": v(-0.51, 8.44) * mm});
            skLineSegment(sketch, "E205", {"start": v(-0.51, 8.44) * mm, "end": v(0.04, 9.4) * mm});
            skPoint(sketch, "E206.second.point", {"position": v(-8.55, 17.78) * mm});
            skPoint(sketch, "E206.third.point", {"position": v(-4.15, 17.78) * mm});
            skLineSegment(sketch, "E207.0", {"start": v(-10.71, 21.47) * mm, "end": v(-1.91, 21.47) * mm});
            skLineSegment(sketch, "E207.1", {"start": v(-1.91, 21.47) * mm, "end": v(-6.31, 13.85) * mm});
            skLineSegment(sketch, "E207.2", {"start": v(-6.31, 13.85) * mm, "end": v(-10.71, 21.47) * mm});
            skPoint(sketch, "E207.0.midPoint", {"position": v(-6.31, 21.47) * mm});
            skLineSegment(sketch, "E208", {"start": v(-4.11, 17.66) * mm, "end": v(-8.51, 17.66) * mm});
            skLineSegment(sketch, "E209", {"start": v(-8.51, 17.66) * mm, "end": v(-6.31, 21.47) * mm});
            skLineSegment(sketch, "E210", {"start": v(-4.11, 17.66) * mm, "end": v(-6.31, 21.47) * mm});
            skLineSegment(sketch, "E211", {"start": v(-6.31, 17.66) * mm, "end": v(-5.21, 15.76) * mm});
            skLineSegment(sketch, "E212", {"start": v(-5.21, 15.76) * mm, "end": v(-7.41, 15.76) * mm});
            skLineSegment(sketch, "E213", {"start": v(-7.41, 15.76) * mm, "end": v(-6.31, 17.66) * mm});
            skLineSegment(sketch, "E214", {"start": v(-7.41, 19.57) * mm, "end": v(-8.51, 21.47) * mm});
            skLineSegment(sketch, "E215", {"start": v(-8.51, 21.47) * mm, "end": v(-9.61, 19.57) * mm});
            skLineSegment(sketch, "E216", {"start": v(-9.61, 19.57) * mm, "end": v(-7.41, 19.57) * mm});
            skLineSegment(sketch, "E217", {"start": v(-5.21, 19.57) * mm, "end": v(-3.01, 19.57) * mm});
            skLineSegment(sketch, "E218", {"start": v(-3.01, 19.57) * mm, "end": v(-4.11, 21.47) * mm});
            skLineSegment(sketch, "E219", {"start": v(-4.11, 21.47) * mm, "end": v(-5.21, 19.57) * mm});
            skLineSegment(sketch, "E220", {"start": v(-4.11, 19.57) * mm, "end": v(-3.56, 18.62) * mm});
            skLineSegment(sketch, "E221", {"start": v(-3.56, 18.62) * mm, "end": v(-4.66, 18.62) * mm});
            skLineSegment(sketch, "E222", {"start": v(-4.66, 18.62) * mm, "end": v(-4.11, 19.57) * mm});
            skLineSegment(sketch, "E223", {"start": v(-3.56, 20.52) * mm, "end": v(-2.46, 20.52) * mm});
            skLineSegment(sketch, "E224", {"start": v(-2.46, 20.52) * mm, "end": v(-3.01, 21.47) * mm});
            skLineSegment(sketch, "E225", {"start": v(-3.01, 21.47) * mm, "end": v(-3.56, 20.52) * mm});
            skLineSegment(sketch, "E226", {"start": v(-4.66, 20.52) * mm, "end": v(-5.76, 20.52) * mm});
            skLineSegment(sketch, "E227", {"start": v(-5.76, 20.52) * mm, "end": v(-5.21, 21.47) * mm});
            skLineSegment(sketch, "E228", {"start": v(-5.21, 21.47) * mm, "end": v(-4.66, 20.52) * mm});
            skLineSegment(sketch, "E229", {"start": v(-6.86, 20.52) * mm, "end": v(-7.96, 20.52) * mm});
            skLineSegment(sketch, "E230", {"start": v(-7.96, 20.52) * mm, "end": v(-7.41, 21.47) * mm});
            skLineSegment(sketch, "E231", {"start": v(-7.41, 21.47) * mm, "end": v(-6.86, 20.52) * mm});
            skLineSegment(sketch, "E232", {"start": v(-9.06, 20.52) * mm, "end": v(-10.16, 20.52) * mm});
            skLineSegment(sketch, "E233", {"start": v(-10.16, 20.52) * mm, "end": v(-9.61, 21.47) * mm});
            skLineSegment(sketch, "E234", {"start": v(-9.61, 21.47) * mm, "end": v(-9.06, 20.52) * mm});
            skLineSegment(sketch, "E235", {"start": v(-8.51, 19.57) * mm, "end": v(-9.06, 18.62) * mm});
            skLineSegment(sketch, "E236", {"start": v(-9.06, 18.62) * mm, "end": v(-7.96, 18.62) * mm});
            skLineSegment(sketch, "E237", {"start": v(-7.96, 18.62) * mm, "end": v(-8.51, 19.57) * mm});
            skLineSegment(sketch, "E238", {"start": v(-6.86, 16.71) * mm, "end": v(-7.41, 17.66) * mm});
            skLineSegment(sketch, "E239", {"start": v(-7.41, 17.66) * mm, "end": v(-7.96, 16.71) * mm});
            skLineSegment(sketch, "E240", {"start": v(-7.96, 16.71) * mm, "end": v(-6.86, 16.71) * mm});
            skLineSegment(sketch, "E241", {"start": v(-5.76, 16.71) * mm, "end": v(-5.21, 17.66) * mm});
            skLineSegment(sketch, "E242", {"start": v(-5.21, 17.66) * mm, "end": v(-4.66, 16.71) * mm});
            skLineSegment(sketch, "E243", {"start": v(-4.66, 16.71) * mm, "end": v(-5.76, 16.71) * mm});
            skLineSegment(sketch, "E244", {"start": v(-6.31, 15.76) * mm, "end": v(-5.76, 14.8) * mm});
            skLineSegment(sketch, "E245", {"start": v(-5.76, 14.8) * mm, "end": v(-6.86, 14.8) * mm});
            skLineSegment(sketch, "E246", {"start": v(-6.86, 14.8) * mm, "end": v(-6.31, 15.76) * mm});
            skLineSegment(sketch, "E247", {"start": v(7.45, 6.99) * mm, "end": v(6.35, 5.08) * mm});
            skLineSegment(sketch, "E248", {"start": v(5.25, 6.99) * mm, "end": v(6.35, 5.08) * mm});
            skLineSegment(sketch, "E249", {"start": v(5.25, 6.99) * mm, "end": v(7.45, 6.99) * mm});
            skLineSegment(sketch, "E250", {"start": v(0.04, 11.3) * mm, "end": v(1.14, 13.2) * mm});
            skLineSegment(sketch, "E251", {"start": v(-1.06, 13.2) * mm, "end": v(1.14, 13.2) * mm});
            skLineSegment(sketch, "E252", {"start": v(0.04, 11.3) * mm, "end": v(-1.06, 13.2) * mm});
            skLineSegment(sketch, "E253", {"start": v(-6.31, 17.66) * mm, "end": v(-5.21, 19.57) * mm});
            skLineSegment(sketch, "E254", {"start": v(-7.41, 19.57) * mm, "end": v(-5.21, 19.57) * mm});
            skLineSegment(sketch, "E255", {"start": v(-6.31, 17.66) * mm, "end": v(-7.41, 19.57) * mm});
            skSolve(sketch);
        }
        {
            var Q0;
            Q0=makeQuery(id+"F17.imprint","IMPRINT",FACE,{"disambiguationData":[TD([[makeQuery(id+"F17.imprint","IMPRINT",EDGE,{"derivedFrom":sQuery(id+"F17.wireOp",EDGE,"E160")}),-1.0]])]});
            var Q1;
            Q1=makeQuery(id+"F17.imprint","IMPRINT",FACE,{"disambiguationData":[TD([[makeQuery(id+"F17.imprint","IMPRINT",EDGE,{"derivedFrom":sQuery(id+"F17.wireOp",EDGE,"E163")}),-1.0]])]});
            var Q2;
            Q2=makeQuery(id+"F17.imprint","IMPRINT",FACE,{"disambiguationData":[TD([[makeQuery(id+"F17.imprint","IMPRINT",EDGE,{"derivedFrom":sQuery(id+"F17.wireOp",EDGE,"E157")}),1.0]])]});
            var Q3;
            Q3=makeQuery(id+"F17.imprint","IMPRINT",FACE,{"disambiguationData":[TD([[makeQuery(id+"F17.imprint","IMPRINT",EDGE,{"derivedFrom":sQuery(id+"F17.wireOp",EDGE,"E154")}),1.0]])]});
            var Q4;
            Q4=makeQuery(id+"F17.imprint","IMPRINT",FACE,{"disambiguationData":[TD([[makeQuery(id+"F17.imprint","IMPRINT",EDGE,{"derivedFrom":sQuery(id+"F17.wireOp",EDGE,"E148")}),-1.0]])]});
            var Q5;
            Q5=makeQuery(id+"F17.imprint","IMPRINT",FACE,{"disambiguationData":[TD([[makeQuery(id+"F17.imprint","IMPRINT",EDGE,{"derivedFrom":sQuery(id+"F17.wireOp",EDGE,"E151")}),-1.0]])]});
            var Q6;
            Q6=makeQuery(id+"F17.imprint","IMPRINT",FACE,{"disambiguationData":[TD([[makeQuery(id+"F17.imprint","IMPRINT",EDGE,{"derivedFrom":sQuery(id+"F17.wireOp",EDGE,"E145")}),-1.0]])]});
            var Q7;
            Q7=makeQuery(id+"F17.imprint","IMPRINT",FACE,{"disambiguationData":[TD([[makeQuery(id+"F17.imprint","IMPRINT",EDGE,{"derivedFrom":sQuery(id+"F17.wireOp",EDGE,"E139")}),-1.0]])]});
            var Q8;
            Q8=makeQuery(id+"F17.imprint","IMPRINT",FACE,{"disambiguationData":[TD([[makeQuery(id+"F17.imprint","IMPRINT",EDGE,{"derivedFrom":sQuery(id+"F17.wireOp",EDGE,"E142")}),1.0]])]});
            var Q9;
            Q9=makeQuery(id+"F17.imprint","IMPRINT",FACE,{"disambiguationData":[TD([[makeQuery(id+"F17.imprint","IMPRINT",EDGE,{"derivedFrom":sQuery(id+"F17.wireOp",EDGE,"E203")}),-1.0]])]});
            var Q10;
            Q10=makeQuery(id+"F17.imprint","IMPRINT",FACE,{"disambiguationData":[TD([[makeQuery(id+"F17.imprint","IMPRINT",EDGE,{"derivedFrom":sQuery(id+"F17.wireOp",EDGE,"E200")}),-1.0]])]});
            var Q11;
            Q11=makeQuery(id+"F17.imprint","IMPRINT",FACE,{"disambiguationData":[TD([[makeQuery(id+"F17.imprint","IMPRINT",EDGE,{"derivedFrom":sQuery(id+"F17.wireOp",EDGE,"E197")}),1.0]])]});
            var Q12;
            Q12=makeQuery(id+"F17.imprint","IMPRINT",FACE,{"disambiguationData":[TD([[makeQuery(id+"F17.imprint","IMPRINT",EDGE,{"derivedFrom":sQuery(id+"F17.wireOp",EDGE,"E194")}),1.0]])]});
            var Q13;
            Q13=makeQuery(id+"F17.imprint","IMPRINT",FACE,{"disambiguationData":[TD([[makeQuery(id+"F17.imprint","IMPRINT",EDGE,{"derivedFrom":sQuery(id+"F17.wireOp",EDGE,"E188")}),-1.0]])]});
            var Q14;
            Q14=makeQuery(id+"F17.imprint","IMPRINT",FACE,{"disambiguationData":[TD([[makeQuery(id+"F17.imprint","IMPRINT",EDGE,{"derivedFrom":sQuery(id+"F17.wireOp",EDGE,"E191")}),-1.0]])]});
            var Q15;
            Q15=makeQuery(id+"F17.imprint","IMPRINT",FACE,{"disambiguationData":[TD([[makeQuery(id+"F17.imprint","IMPRINT",EDGE,{"derivedFrom":sQuery(id+"F17.wireOp",EDGE,"E179")}),-1.0]])]});
            var Q16;
            Q16=makeQuery(id+"F17.imprint","IMPRINT",FACE,{"disambiguationData":[TD([[makeQuery(id+"F17.imprint","IMPRINT",EDGE,{"derivedFrom":sQuery(id+"F17.wireOp",EDGE,"E182")}),1.0]])]});
            var Q17;
            Q17=makeQuery(id+"F17.imprint","IMPRINT",FACE,{"disambiguationData":[TD([[makeQuery(id+"F17.imprint","IMPRINT",EDGE,{"derivedFrom":sQuery(id+"F17.wireOp",EDGE,"E185")}),-1.0]])]});
            var Q18;
            Q18=makeQuery(id+"F17.imprint","IMPRINT",FACE,{"disambiguationData":[TD([[makeQuery(id+"F17.imprint","IMPRINT",EDGE,{"derivedFrom":sQuery(id+"F17.wireOp",EDGE,"E244")}),-1.0]])]});
            var Q19;
            Q19=makeQuery(id+"F17.imprint","IMPRINT",FACE,{"disambiguationData":[TD([[makeQuery(id+"F17.imprint","IMPRINT",EDGE,{"derivedFrom":sQuery(id+"F17.wireOp",EDGE,"E241")}),-1.0]])]});
            var Q20;
            Q20=makeQuery(id+"F17.imprint","IMPRINT",FACE,{"disambiguationData":[TD([[makeQuery(id+"F17.imprint","IMPRINT",EDGE,{"derivedFrom":sQuery(id+"F17.wireOp",EDGE,"E238")}),1.0]])]});
            var Q21;
            Q21=makeQuery(id+"F17.imprint","IMPRINT",FACE,{"disambiguationData":[TD([[makeQuery(id+"F17.imprint","IMPRINT",EDGE,{"derivedFrom":sQuery(id+"F17.wireOp",EDGE,"E235")}),1.0]])]});
            var Q22;
            Q22=makeQuery(id+"F17.imprint","IMPRINT",FACE,{"disambiguationData":[TD([[makeQuery(id+"F17.imprint","IMPRINT",EDGE,{"derivedFrom":sQuery(id+"F17.wireOp",EDGE,"E229")}),-1.0]])]});
            var Q23;
            Q23=makeQuery(id+"F17.imprint","IMPRINT",FACE,{"disambiguationData":[TD([[makeQuery(id+"F17.imprint","IMPRINT",EDGE,{"derivedFrom":sQuery(id+"F17.wireOp",EDGE,"E232")}),-1.0]])]});
            var Q24;
            Q24=makeQuery(id+"F17.imprint","IMPRINT",FACE,{"disambiguationData":[TD([[makeQuery(id+"F17.imprint","IMPRINT",EDGE,{"derivedFrom":sQuery(id+"F17.wireOp",EDGE,"E220")}),-1.0]])]});
            var Q25;
            Q25=makeQuery(id+"F17.imprint","IMPRINT",FACE,{"disambiguationData":[TD([[makeQuery(id+"F17.imprint","IMPRINT",EDGE,{"derivedFrom":sQuery(id+"F17.wireOp",EDGE,"E223")}),1.0]])]});
            var Q26;
            Q26=makeQuery(id+"F17.imprint","IMPRINT",FACE,{"disambiguationData":[TD([[makeQuery(id+"F17.imprint","IMPRINT",EDGE,{"derivedFrom":sQuery(id+"F17.wireOp",EDGE,"E226")}),-1.0]])]});
            var Q27;
            Q27=makeQuery(id+"F17.imprint","IMPRINT",FACE,{"disambiguationData":[TD([[makeQuery(id+"F17.imprint","IMPRINT",EDGE,{"derivedFrom":sQuery(id+"F17.wireOp",EDGE,"E253")}),1.0]])]});
            var Q28;
            Q28=makeQuery(id+"F17.imprint","IMPRINT",FACE,{"disambiguationData":[TD([[makeQuery(id+"F17.imprint","IMPRINT",EDGE,{"derivedFrom":sQuery(id+"F17.wireOp",EDGE,"E250")}),1.0]])]});
            var Q29;
            Q29=makeQuery(id+"F17.imprint","IMPRINT",FACE,{"disambiguationData":[TD([[makeQuery(id+"F17.imprint","IMPRINT",EDGE,{"derivedFrom":sQuery(id+"F17.wireOp",EDGE,"E247")}),-1.0]])]});
            extrude(context, id + "F18", {"entities" : qUnion([Q0, Q1, Q2, Q3, Q4, Q5, Q6, Q7, Q8, Q9, Q10, Q11, Q12, Q13, Q14, Q15, Q16, Q17, Q18, Q19, Q20, Q21, Q22, Q23, Q24, Q25, Q26, Q27, Q28, Q29]), "operationType" : NewBodyOperationType.REMOVE, "oppositeDirection" : true, "depth" : 2.54 * mm});
        }
        {
            var Q0;
            Q0=makeQuery(id+"F1.opExtrude","SWEPT_FACE",FACE,{"disambiguationData":[OSD([sQuery(id+"F0.wireOp",EDGE,"E0.right")])]});
            var sketch = newSketch(context, id + "F19", { "sketchPlane" : qUnion([Q0])});
            skPoint(sketch, "E256.cCircle.perimeterSnap0", {"position": v(12.85, 0) * mm});
            skLineSegment(sketch, "E256.0", {"start": v(19.93, 5.14) * mm, "end": v(19.93, 1.78) * mm});
            skLineSegment(sketch, "E256.1", {"start": v(19.93, -5.14) * mm, "end": v(16.92, -6.12) * mm});
            skLineSegment(sketch, "E256.2", {"start": v(10.15, -8.32) * mm, "end": v(8.38, -5.88) * mm});
            skLineSegment(sketch, "E256.3", {"start": v(4.1, 0) * mm, "end": v(5.91, 2.48) * mm});
            skLineSegment(sketch, "E256.4", {"start": v(10.15, 8.32) * mm, "end": v(13.01, 7.39) * mm});
            skPoint(sketch, "E256.0.midPoint", {"position": v(19.93, 0) * mm});
            skPoint(sketch, "E256.0.midPoint.positionSnap0", {"position": v(12.85, 0) * mm});
            skArc(sketch, "E257", {"start": v(5.91, 2.48) * mm, "mid": v(1.04, 0) * mm, "end": v(5.91, -2.48) * mm});
            skArc(sketch, "E258", {"start": v(8.38, -5.88) * mm, "mid": v(9.22, -11.18) * mm, "end": v(13.01, -7.39) * mm});
            skArc(sketch, "E259", {"start": v(16.92, -6.12) * mm, "mid": v(22.49, -7) * mm, "end": v(19.93, -1.98) * mm});
            skArc(sketch, "E260", {"start": v(19.93, 1.78) * mm, "mid": v(22.64, 7.11) * mm, "end": v(16.73, 6.18) * mm});
            skArc(sketch, "E261", {"start": v(12.94, 7.18) * mm, "mid": v(9.32, 11.2) * mm, "end": v(8.38, 5.88) * mm});
            skLineSegment(sketch, "E262.trimOffspring", {"start": v(16.73, 6.18) * mm, "end": v(19.93, 5.14) * mm});
            skLineSegment(sketch, "E263.trimOffspring", {"start": v(19.93, -1.98) * mm, "end": v(19.93, -5.14) * mm});
            skLineSegment(sketch, "E264.trimOffspring", {"start": v(13.01, -7.39) * mm, "end": v(10.15, -8.32) * mm});
            skLineSegment(sketch, "E265.trimOffspring", {"start": v(5.91, -2.48) * mm, "end": v(4.1, 0) * mm});
            skLineSegment(sketch, "E266.trimOffspring", {"start": v(8.38, 5.88) * mm, "end": v(10.15, 8.32) * mm});
            skSolve(sketch);
        }
        {
            var Q0;
            Q0=makeQuery(id+"F19.imprint","IMPRINT",FACE,{"disambiguationData":[TD([[makeQuery(id+"F19.imprint","IMPRINT",EDGE,{"derivedFrom":sQuery(id+"F19.wireOp",EDGE,"E256.2")}),1.0]])]});
            var Q1;
            Q1=makeQuery(id+"F19.imprint","IMPRINT",FACE,{"disambiguationData":[TD([[makeQuery(id+"F19.imprint","IMPRINT",EDGE,{"derivedFrom":sQuery(id+"F19.wireOp",EDGE,"E256.3")}),1.0]])]});
            var Q2;
            {var subQ0=sQuery(id+"F19.wireOp",EDGE,"E256.4");Q2=makeQuery(id+"F19.imprint","IMPRINT",FACE,{"disambiguationData":[TD([[makeQuery(id+"F19.imprint","IMPRINT",EDGE,{"derivedFrom":subQ0}),1.0]])]});}
            var Q3;
            Q3=makeQuery(id+"F19.imprint","IMPRINT",FACE,{"disambiguationData":[TD([[makeQuery(id+"F19.imprint","IMPRINT",EDGE,{"derivedFrom":sQuery(id+"F19.wireOp",EDGE,"E256.0")}),1.0]])]});
            var Q4;
            Q4=makeQuery(id+"F19.imprint","IMPRINT",FACE,{"disambiguationData":[TD([[makeQuery(id+"F19.imprint","IMPRINT",EDGE,{"derivedFrom":sQuery(id+"F19.wireOp",EDGE,"E256.1")}),1.0]])]});
            extrude(context, id + "F20", {"entities" : qUnion([Q0, Q1, Q2, Q3, Q4]), "operationType" : NewBodyOperationType.REMOVE, "oppositeDirection" : true, "depth" : 2.54 * mm});
        }
        {
            var Q0;
            Q0=makeQuery(id+"F1.opExtrude","CAP_FACE",FACE,{"disambiguationData":[OSD([sQuery(id+"F0.wireOp",EDGE,"E0.bottom"),sQuery(id+"F0.wireOp",EDGE,"E0.top"),sQuery(id+"F0.wireOp",EDGE,"E0.left"),sQuery(id+"F0.wireOp",EDGE,"E0.right"),sQuery(id+"F0.wireOp",EDGE,"ffxhiTFt-cJhM-8va8-o5as-TkoKFeYBlZlv"),sQuery(id+"F0.wireOp",EDGE,"n15qH9Pv-QceR-e55J-xRJA-4Z23myPxkwqh"),sQuery(id+"F0.wireOp",EDGE,"Tw14qS9G-7LKB-szX9-mnEh-GGdI6fmKwQ57"),sQuery(id+"F0.wireOp",EDGE,"i75eDPNT-zkQp-M9GV-G1os-5atVE6ZioN9H"),sQuery(id+"F0.wireOp",EDGE,"twlR4qeh-pLNo-oQQC-zrHb-Cr716ABeDlEO"),sQuery(id+"F0.wireOp",EDGE,"c9E78YFX-uoQ2-b4qo-jO5v-nr7yERCXFzAn")])],"isStart":false});
            var sketch = newSketch(context, id + "F21", { "sketchPlane" : qUnion([Q0])});
            skPoint(sketch, "E267.middle", {"position": v(-0.12, -0.05) * mm});
            skArc(sketch, "E268", {"start": v(10.04, -0.05) * mm, "mid": v(-0.12, 3.76) * mm, "end": v(-10.28, -0.05) * mm});
            skArc(sketch, "E269", {"start": v(-10.28, -0.05) * mm, "mid": v(-0.12, -3.86) * mm, "end": v(10.04, -0.05) * mm});
            skArc(sketch, "E270", {"start": v(0.5, -3.81) * mm, "mid": v(3.7, -0.01) * mm, "end": v(0.41, 3.72) * mm});
            skArc(sketch, "E271", {"start": v(9.6, 2.65) * mm, "mid": v(-0.12, 4.97) * mm, "end": v(-9.84, 2.66) * mm});
            skLineSegment(sketch, "E272", {"start": v(-9.84, 2.66) * mm, "end": v(-8.25, 6.56) * mm});
            skPoint(sketch, "E273.startSnap0", {"position": v(-0.12, 4.97) * mm});
            skLineSegment(sketch, "E274", {"start": v(9.6, 2.65) * mm, "end": v(7.69, 6.85) * mm});
            skArc(sketch, "E275", {"start": v(-8.25, 6.56) * mm, "mid": v(-0.26, 5.44) * mm, "end": v(7.69, 6.85) * mm});
            skArc(sketch, "E276", {"start": v(0.5, -3.81) * mm, "mid": v(1.55, -0.04) * mm, "end": v(0.41, 3.72) * mm});
            skArc(sketch, "E277", {"start": v(-0.63, 3.72) * mm, "mid": v(-1.74, -0.04) * mm, "end": v(-0.71, -3.82) * mm});
            skArc(sketch, "E278.trimOffspring", {"start": v(-0.63, 3.72) * mm, "mid": v(-3.93, -0.01) * mm, "end": v(-0.71, -3.82) * mm});
            skSolve(sketch);
        }
        {
            var Q0;
            Q0=makeQuery(id+"F21.imprint","IMPRINT",FACE,{"disambiguationData":[TD([[makeQuery(id+"F21.imprint","IMPRINT",EDGE,{"derivedFrom":sQuery(id+"F21.wireOp",EDGE,"E268")}),1.0]])]});
            var Q1;
            Q1=makeQuery(id+"F21.imprint","IMPRINT",FACE,{"disambiguationData":[TD([[makeQuery(id+"F21.imprint","IMPRINT",EDGE,{"derivedFrom":sQuery(id+"F21.wireOp",EDGE,"E271")}),-1.0]])]});
            extrude(context, id + "F22", {"entities" : qUnion([Q0, Q1]), "operationType" : NewBodyOperationType.REMOVE, "oppositeDirection" : true, "depth" : 2.54 * mm});
        }
        {
            var Q0;
            Q0=makeQuery(id+"F22.boolean.opBoolean","COPY",EDGE,{"derivedFrom":makeQuery(id+"F22.opExtrude","CAP_EDGE",EDGE,{"disambiguationData":[OSD([sQuery(id+"F21.wireOp",EDGE,"E276")])],"isStart":true})});
            var Q1;
            Q1=makeQuery(id+"F22.boolean.opBoolean","COPY",EDGE,{"derivedFrom":makeQuery(id+"F22.opExtrude","CAP_EDGE",EDGE,{"disambiguationData":[OSD([sQuery(id+"F21.wireOp",EDGE,"E270")])],"isStart":true})});
            fillet(context, id + "F23", {"entities" : qUnion([Q0, Q1]), "radius" : 0.25 * mm, "allowEdgeOverflow" : false});
        }
    });
